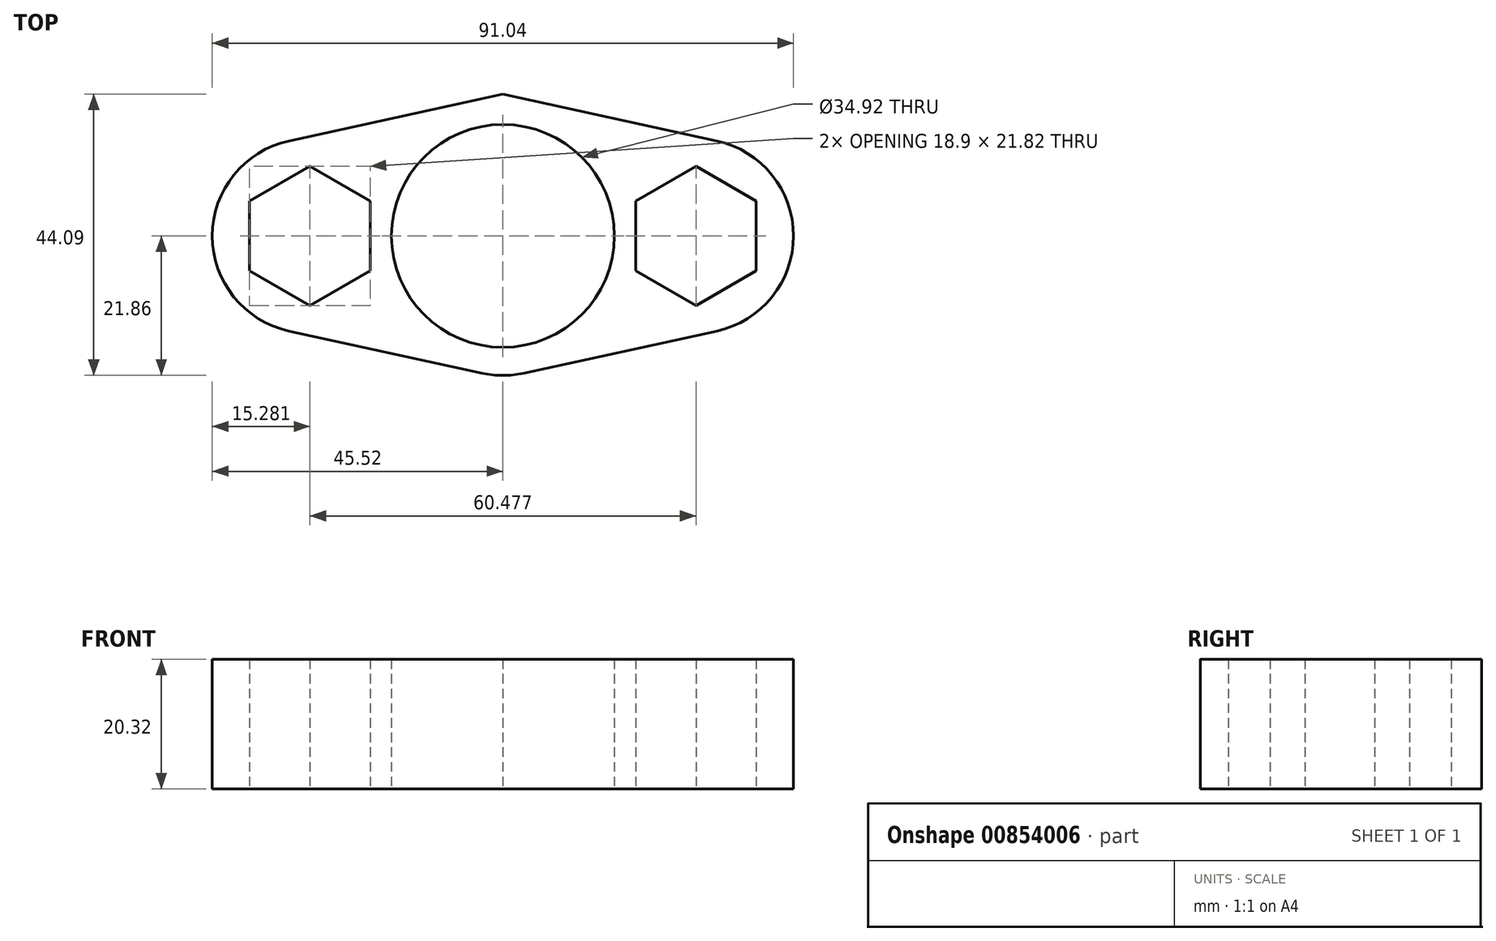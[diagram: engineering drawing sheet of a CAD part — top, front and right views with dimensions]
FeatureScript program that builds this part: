
annotation { "Feature Type Name" : "Feature", "Feature Type Description" : "" }
export const myFeature = defineFeature(function(context is Context, id is Id, definition is map)
    precondition{}
    {
        {
            var Q0;
            Q0=qCreatedBy(makeId("Top.planeOp"),FACE);
            var sketch = newSketch(context, id + "F0", { "sketchPlane" : qUnion([Q0])});
            skCircle(sketch, "E0", {"center": v(0, 0) * mm, "radius": 17.46 * mm});
            skCircle(sketch, "E1.cCircle", {"center": v(-30.24, 0) * mm, "radius": 9.45 * mm, "construction": true});
            skLineSegment(sketch, "E1.0", {"start": v(-39.69, -5.46) * mm, "end": v(-39.69, 5.46) * mm});
            skLineSegment(sketch, "E1.1", {"start": v(-39.69, 5.46) * mm, "end": v(-30.24, 10.91) * mm});
            skLineSegment(sketch, "E1.2", {"start": v(-30.24, 10.91) * mm, "end": v(-20.79, 5.46) * mm});
            skLineSegment(sketch, "E1.3", {"start": v(-20.79, 5.46) * mm, "end": v(-20.79, -5.46) * mm});
            skLineSegment(sketch, "E1.4", {"start": v(-20.79, -5.46) * mm, "end": v(-30.24, -10.91) * mm});
            skLineSegment(sketch, "E1.5", {"start": v(-30.24, -10.91) * mm, "end": v(-39.69, -5.46) * mm});
            skPoint(sketch, "E1.0.midPoint", {"position": v(-39.69, 0) * mm});
            skLineSegment(sketch, "E2", {"start": v(0, 0) * mm, "end": v(0, 22.23) * mm, "construction": true});
            skLineSegment(sketch, "E3.MirrorCS", {"start": v(20.79, 5.46) * mm, "end": v(20.79, -5.46) * mm});
            skLineSegment(sketch, "E4.MirrorCS", {"start": v(39.69, 5.46) * mm, "end": v(30.24, 10.91) * mm});
            skLineSegment(sketch, "E5.MirrorCS", {"start": v(39.69, -5.46) * mm, "end": v(39.69, 5.46) * mm});
            skLineSegment(sketch, "E6.MirrorCS", {"start": v(30.24, 10.91) * mm, "end": v(20.79, 5.46) * mm});
            skLineSegment(sketch, "E7.MirrorCS", {"start": v(20.79, -5.46) * mm, "end": v(30.24, -10.91) * mm});
            skLineSegment(sketch, "E8.MirrorCS", {"start": v(30.24, -10.91) * mm, "end": v(39.69, -5.46) * mm});
            skCircle(sketch, "E9.MirrorC", {"center": v(30.24, 0) * mm, "radius": 9.45 * mm, "construction": true});
            skPoint(sketch, "E10.MirrorP", {"position": v(39.69, 0) * mm});
            skLineSegment(sketch, "E11", {"start": v(0, 22.23) * mm, "end": v(101.6, 0) * mm});
            skLineSegment(sketch, "E12", {"start": v(101.6, 0) * mm, "end": v(0, 22.23) * mm});
            skLineSegment(sketch, "E13", {"start": v(-59.36, 0) * mm, "end": v(0, 0) * mm, "construction": true});
            skLineSegment(sketch, "E14.MirrorCS", {"start": v(101.6, 0) * mm, "end": v(0, -22.23) * mm});
            skLineSegment(sketch, "E15.MirrorCS", {"start": v(-101.6, 0) * mm, "end": v(0, 22.23) * mm});
            skLineSegment(sketch, "E16.MirrorCS", {"start": v(-101.6, 0) * mm, "end": v(0, -22.23) * mm});
            skSolve(sketch);
        }
        {
            var Q0;
            Q0=makeQuery(id+"F0.imprint","IMPRINT",FACE,{"disambiguationData":[TD([[makeQuery(id+"F0.imprint","IMPRINT",EDGE,{"derivedFrom":sQuery(id+"F0.wireOp",EDGE,"E0")}),-1.0]])]});
            extrude(context, id + "F1", {"entities" : qUnion([Q0]), "depth" : 20.32 * mm, "offsetDistance" : 25.4 * mm});
        }
        {
            var Q0;
            Q0=makeQuery(id+"F1.opExtrude","SWEPT_EDGE",EDGE,{"disambiguationData":[OSD([sQuery(id+"F0.wireOp",EDGE,"E12"),sQuery(id+"F0.wireOp",EDGE,"E14.MirrorCS")])]});
            var Q1;
            Q1=makeQuery(id+"F1.opExtrude","SWEPT_EDGE",EDGE,{"disambiguationData":[OSD([sQuery(id+"F0.wireOp",EDGE,"E15.MirrorCS"),sQuery(id+"F0.wireOp",EDGE,"E16.MirrorCS")])]});
            fillet(context, id + "F2", {"entities" : qUnion([Q0, Q1]), "radius" : 15.24 * mm, "tangentPropagation" : true, "allowEdgeOverflow" : false});
        }
    });
